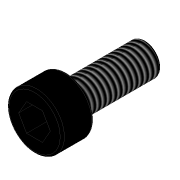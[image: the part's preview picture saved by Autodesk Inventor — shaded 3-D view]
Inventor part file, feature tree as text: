
AUTODESK INVENTOR PART (.ipt)
format: ipt  version: 2020 (Build 240168000, 168)  size: 128,512 bytes
history: native  units: mm
features: extrude x3, sketch x3, fillet x1, thread x1
ambient origin geometry x8: Origin, YZ Plane, XZ Plane, XY Plane, X Axis, Y Axis, Z Axis, Center Point
bodies: Solid1 (feature_tree)
feature tree (8):
  extrude  "Extrusion1"  Depth=2.6mm
  extrude  "Extrusion2"  Depth=1.0mm TaperAngle=0.0deg
  extrude  "Extrusion3"  Depth=7.5mm TaperAngle=0.0deg
  fillet  "Fillet1"  Radius=0.2mm
  thread  "Thread1"  [1 undecoded]
  sketch  "Sketch1"  dims[d0=5.25mm d1=2.6mm]
  sketch  "Sketch2"  dims[d2=2.0mm d3=0.0mm d4=1.0mm d5=0.0mm]
  sketch  "Sketch3"  dims[d6=3.0mm d7=7.5mm d8=0.0mm d9=0.2mm d10=7.3mm d11=0.0mm]
note: 1 required parameter value undecoded (feature->parameter linkage not recoverable at this tier; creation-order binding heuristic only, values carry confidence <= 0.55)
